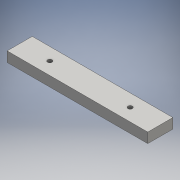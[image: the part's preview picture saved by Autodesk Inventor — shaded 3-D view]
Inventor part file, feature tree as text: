
AUTODESK INVENTOR PART (.ipt)
format: ipt  version: 2016 (Build 200138000, 138)  size: 96,768 bytes
history: native  units: mm
features: sketch x2, extrude x1, hole x1
ambient origin geometry x8: Origin, YZ Plane, XZ Plane, XY Plane, X Axis, Y Axis, Z Axis, Center Point
bodies: Solid1 (feature_tree)
feature tree (4):
  extrude  "Extrusion1"  Depth=25.0mm
  hole  "Hole1"  [1 undecoded]
  sketch  "Sketch1"  dims[d0=140.0mm d1=25.0mm]
  sketch  "Sketch2"  dims[d2=70.0mm d3=12.5mm d4=10.0mm d5=0.0mm d6=80.0mm d7=40.0mm d8=4.5mm d9=6.0mm d10=4.0mm d11=2.0mm d12=90.0deg d13=8.0mm d14=20.594885mm]
note: 1 required parameter value undecoded (feature->parameter linkage not recoverable at this tier; creation-order binding heuristic only, values carry confidence <= 0.55)
